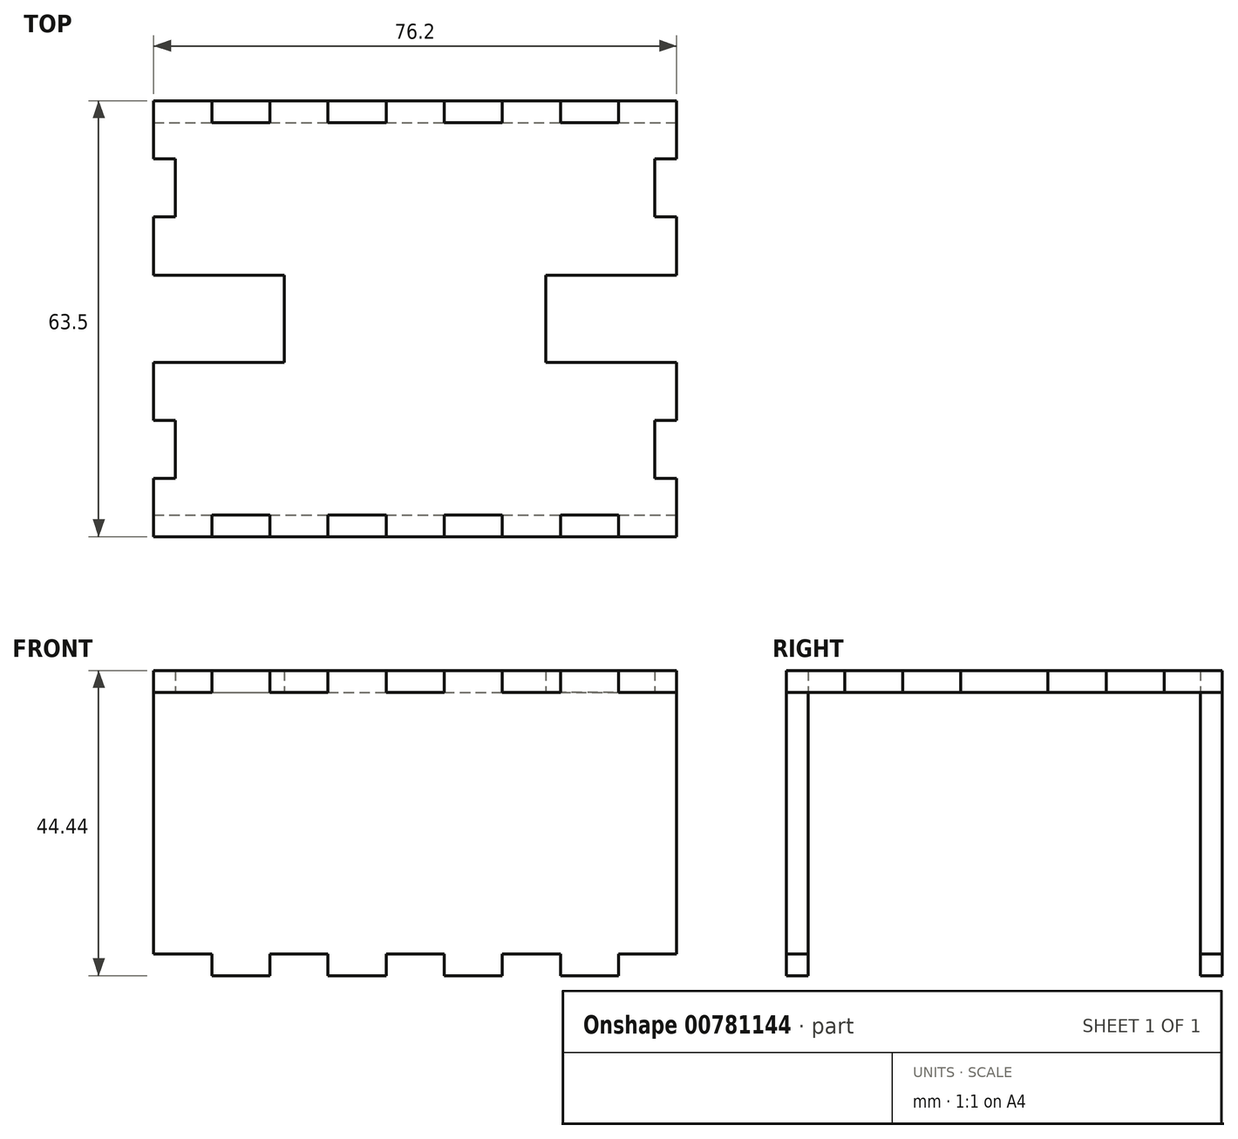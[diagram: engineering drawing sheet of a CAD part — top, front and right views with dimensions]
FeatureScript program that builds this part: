
annotation { "Feature Type Name" : "Feature", "Feature Type Description" : "" }
export const myFeature = defineFeature(function(context is Context, id is Id, definition is map)
    precondition{}
    {
        {
            var Q0;
            Q0=qCreatedBy(makeId("Top.planeOp"),FACE);
            var sketch = newSketch(context, id + "F0", { "sketchPlane" : qUnion([Q0])});
            skLineSegment(sketch, "E0.bottom", {"start": v(38.1, 31.75) * mm, "end": v(29.63, 31.75) * mm});
            skLineSegment(sketch, "E0.top", {"start": v(38.1, -31.75) * mm, "end": v(29.63, -31.75) * mm});
            skLineSegment(sketch, "E0.left", {"start": v(38.1, 31.75) * mm, "end": v(38.1, 23.28) * mm});
            skLineSegment(sketch, "E0.right", {"start": v(-38.1, 31.75) * mm, "end": v(-38.1, 23.28) * mm});
            skPoint(sketch, "E0.middle", {"position": v(0, 0) * mm});
            skLineSegment(sketch, "E1.bottom", {"start": v(-38.1, -31.75) * mm, "end": v(-29.63, -31.75) * mm});
            skLineSegment(sketch, "E1.top", {"start": v(-29.63, -28.58) * mm, "end": v(-21.17, -28.57) * mm});
            skLineSegment(sketch, "E1.right", {"start": v(38.1, -31.75) * mm, "end": v(38.1, -28.57) * mm});
            skLineSegment(sketch, "E2.right", {"start": v(-29.63, -28.58) * mm, "end": v(-29.63, -31.75) * mm});
            skLineSegment(sketch, "E3.bottom", {"start": v(-29.63, -28.58) * mm, "end": v(-21.17, -28.58) * mm});
            skLineSegment(sketch, "E3.right", {"start": v(-21.17, -28.57) * mm, "end": v(-21.17, -31.75) * mm});
            skLineSegment(sketch, "E4.top", {"start": v(-21.17, -31.75) * mm, "end": v(-12.7, -31.75) * mm});
            skLineSegment(sketch, "E4.left", {"start": v(-21.17, -28.58) * mm, "end": v(-21.17, -31.75) * mm});
            skLineSegment(sketch, "E4.right", {"start": v(-12.7, -28.58) * mm, "end": v(-12.7, -31.75) * mm});
            skLineSegment(sketch, "E5.bottom", {"start": v(-12.7, -28.58) * mm, "end": v(-4.23, -28.58) * mm});
            skLineSegment(sketch, "E5.right", {"start": v(-4.23, -28.58) * mm, "end": v(-4.23, -31.75) * mm});
            skLineSegment(sketch, "E6.top", {"start": v(-4.23, -31.75) * mm, "end": v(4.23, -31.75) * mm});
            skLineSegment(sketch, "E6.right", {"start": v(4.23, -28.58) * mm, "end": v(4.23, -31.75) * mm});
            skLineSegment(sketch, "E7.bottom", {"start": v(4.23, -28.58) * mm, "end": v(12.7, -28.58) * mm});
            skLineSegment(sketch, "E7.right", {"start": v(12.7, -28.57) * mm, "end": v(12.7, -31.75) * mm});
            skLineSegment(sketch, "E8.top", {"start": v(12.7, -31.75) * mm, "end": v(21.17, -31.75) * mm});
            skLineSegment(sketch, "E8.left", {"start": v(12.7, -28.58) * mm, "end": v(12.7, -31.75) * mm});
            skLineSegment(sketch, "E8.right", {"start": v(21.17, -28.58) * mm, "end": v(21.17, -31.75) * mm});
            skLineSegment(sketch, "E9.bottom", {"start": v(21.17, -28.58) * mm, "end": v(29.63, -28.58) * mm});
            skLineSegment(sketch, "E9.left", {"start": v(21.17, -28.57) * mm, "end": v(21.17, -31.75) * mm});
            skLineSegment(sketch, "E9.right", {"start": v(29.63, -28.57) * mm, "end": v(29.63, -31.75) * mm});
            skLineSegment(sketch, "E10.bottom", {"start": v(29.63, -31.75) * mm, "end": v(38.1, -31.75) * mm});
            skLineSegment(sketch, "E10.left", {"start": v(29.63, -31.75) * mm, "end": v(29.63, -28.57) * mm});
            skLineSegment(sketch, "E11.trimOffspring", {"start": v(-29.63, -31.75) * mm, "end": v(-38.1, -31.75) * mm});
            skLineSegment(sketch, "E12.trimOffspring", {"start": v(-12.7, -31.75) * mm, "end": v(-21.17, -31.75) * mm});
            skLineSegment(sketch, "E13.trimOffspring", {"start": v(4.23, -31.75) * mm, "end": v(-4.23, -31.75) * mm});
            skLineSegment(sketch, "E14.trimOffspring", {"start": v(21.17, -31.75) * mm, "end": v(12.7, -31.75) * mm});
            skLineSegment(sketch, "E15.MirrorCS", {"start": v(-29.63, 28.58) * mm, "end": v(-21.17, 28.58) * mm});
            skLineSegment(sketch, "E16.MirrorCS", {"start": v(-12.7, 28.58) * mm, "end": v(-4.23, 28.58) * mm});
            skLineSegment(sketch, "E17.MirrorCS", {"start": v(4.23, 28.58) * mm, "end": v(12.7, 28.58) * mm});
            skLineSegment(sketch, "E18.MirrorCS", {"start": v(21.17, 28.58) * mm, "end": v(29.63, 28.58) * mm});
            skLineSegment(sketch, "E19.MirrorCS", {"start": v(29.63, 31.75) * mm, "end": v(38.1, 31.75) * mm});
            skLineSegment(sketch, "E20.MirrorCS", {"start": v(21.17, 31.75) * mm, "end": v(12.7, 31.75) * mm});
            skLineSegment(sketch, "E21.MirrorCS", {"start": v(4.23, 31.75) * mm, "end": v(-4.23, 31.75) * mm});
            skLineSegment(sketch, "E22.MirrorCS", {"start": v(-21.17, 31.75) * mm, "end": v(-12.7, 31.75) * mm});
            skLineSegment(sketch, "E23.MirrorCS", {"start": v(-29.63, 31.75) * mm, "end": v(-38.1, 31.75) * mm});
            skLineSegment(sketch, "E24.MirrorCS", {"start": v(-29.63, 28.58) * mm, "end": v(-29.63, 31.75) * mm});
            skLineSegment(sketch, "E25.MirrorCS", {"start": v(-21.17, 28.58) * mm, "end": v(-21.17, 31.75) * mm});
            skLineSegment(sketch, "E26.MirrorCS", {"start": v(-12.7, 28.58) * mm, "end": v(-12.7, 31.75) * mm});
            skLineSegment(sketch, "E27.MirrorCS", {"start": v(-4.23, 28.58) * mm, "end": v(-4.23, 31.75) * mm});
            skLineSegment(sketch, "E28.MirrorCS", {"start": v(4.23, 28.58) * mm, "end": v(4.23, 31.75) * mm});
            skLineSegment(sketch, "E29.MirrorCS", {"start": v(12.7, 28.58) * mm, "end": v(12.7, 31.75) * mm});
            skLineSegment(sketch, "E30.MirrorCS", {"start": v(21.17, 28.58) * mm, "end": v(21.17, 31.75) * mm});
            skLineSegment(sketch, "E31.MirrorCS", {"start": v(29.63, 28.58) * mm, "end": v(29.63, 31.75) * mm});
            skLineSegment(sketch, "E32.MirrorCS", {"start": v(38.1, 31.75) * mm, "end": v(38.1, 28.57) * mm});
            skLineSegment(sketch, "E33.trimOffspring", {"start": v(-12.7, 31.75) * mm, "end": v(-21.17, 31.75) * mm});
            skLineSegment(sketch, "E34.trimOffspring", {"start": v(-12.7, -28.57) * mm, "end": v(-4.23, -28.57) * mm});
            skLineSegment(sketch, "E35.trimOffspring", {"start": v(4.23, -28.57) * mm, "end": v(12.7, -28.57) * mm});
            skLineSegment(sketch, "E36.trimOffspring", {"start": v(21.17, -28.57) * mm, "end": v(29.63, -28.57) * mm});
            skLineSegment(sketch, "E37.top", {"start": v(-38.12, -31.75) * mm, "end": v(-38.1, -31.75) * mm});
            skLineSegment(sketch, "E38", {"start": v(-34.92, -31.75) * mm, "end": v(-34.92, -6.35) * mm});
            skLineSegment(sketch, "E39.bottom", {"start": v(-38.1, 6.35) * mm, "end": v(-19.05, 6.35) * mm});
            skLineSegment(sketch, "E39.top", {"start": v(-38.1, -6.35) * mm, "end": v(-19.05, -6.35) * mm});
            skLineSegment(sketch, "E39.right", {"start": v(-19.05, 6.35) * mm, "end": v(-19.05, -6.35) * mm});
            skLineSegment(sketch, "E40", {"start": v(-38.1, 14.82) * mm, "end": v(-34.93, 14.82) * mm});
            skLineSegment(sketch, "E41", {"start": v(-38.1, 23.28) * mm, "end": v(-34.93, 23.28) * mm});
            skLineSegment(sketch, "E42", {"start": v(-38.1, 6.35) * mm, "end": v(-34.93, 6.35) * mm});
            skLineSegment(sketch, "E43", {"start": v(-38.1, -23.28) * mm, "end": v(-34.93, -23.28) * mm});
            skLineSegment(sketch, "E44", {"start": v(-34.93, -14.82) * mm, "end": v(-38.1, -14.82) * mm});
            skLineSegment(sketch, "E45", {"start": v(-38.1, -6.35) * mm, "end": v(-34.93, -6.35) * mm});
            skLineSegment(sketch, "E46.trimOffspring", {"start": v(-38.1, 14.82) * mm, "end": v(-38.1, 6.35) * mm});
            skLineSegment(sketch, "E47.trimOffspring", {"start": v(-38.1, -6.35) * mm, "end": v(-38.1, -14.82) * mm});
            skLineSegment(sketch, "E48.trimOffspring", {"start": v(-34.93, 6.35) * mm, "end": v(-34.93, 31.75) * mm});
            skLineSegment(sketch, "E49.trimOffspring", {"start": v(-38.1, -23.28) * mm, "end": v(-38.1, -31.75) * mm});
            skLineSegment(sketch, "E50.MirrorCS", {"start": v(38.1, 23.28) * mm, "end": v(34.93, 23.28) * mm});
            skLineSegment(sketch, "E51.MirrorCS", {"start": v(34.93, 6.35) * mm, "end": v(34.93, 31.75) * mm});
            skLineSegment(sketch, "E52.MirrorCS", {"start": v(38.1, 14.82) * mm, "end": v(34.93, 14.82) * mm});
            skLineSegment(sketch, "E53.MirrorCS", {"start": v(38.1, -6.35) * mm, "end": v(19.05, -6.35) * mm});
            skLineSegment(sketch, "E54.MirrorCS", {"start": v(38.1, 6.35) * mm, "end": v(19.05, 6.35) * mm});
            skLineSegment(sketch, "E55.MirrorCS", {"start": v(34.93, -14.82) * mm, "end": v(38.1, -14.82) * mm});
            skLineSegment(sketch, "E56.MirrorCS", {"start": v(19.05, 6.35) * mm, "end": v(19.05, -6.35) * mm});
            skLineSegment(sketch, "E57.MirrorCS", {"start": v(34.92, -31.75) * mm, "end": v(34.92, -6.35) * mm});
            skLineSegment(sketch, "E58.MirrorCS", {"start": v(38.1, -23.28) * mm, "end": v(34.93, -23.28) * mm});
            skLineSegment(sketch, "E59.trimOffspring", {"start": v(38.1, -23.28) * mm, "end": v(38.1, -31.75) * mm});
            skLineSegment(sketch, "E60.trimOffspring", {"start": v(38.1, -6.35) * mm, "end": v(38.1, -14.82) * mm});
            skLineSegment(sketch, "E61.trimOffspring", {"start": v(38.1, 14.82) * mm, "end": v(38.1, 6.35) * mm});
            skSolve(sketch);
        }
        {
            var Q0;
            Q0 = qSketchRegion(id + "F0", true);
            extrude(context, id + "F1", {"entities" : qUnion([Q0]), "depth" : 3.17 * mm, "offsetDistance" : 25.4 * mm});
        }
        {
            var Q0;
            Q0=makeQuery(id+"F1.opExtrude","SWEPT_FACE",FACE,{"disambiguationData":[OSD([sQuery(id+"F0.wireOp",EDGE,"E3.bottom")])]});
            var sketch = newSketch(context, id + "F2", { "sketchPlane" : qUnion([Q0])});
            skLineSegment(sketch, "E62.bottom", {"start": v(-29.63, 3.18) * mm, "end": v(-21.17, 3.18) * mm});
            skLineSegment(sketch, "E62.top", {"start": v(-29.63, -41.28) * mm, "end": v(-21.17, -41.28) * mm});
            skLineSegment(sketch, "E62.left", {"start": v(-38.1, 3.18) * mm, "end": v(-38.1, -41.28) * mm});
            skLineSegment(sketch, "E62.right", {"start": v(38.1, 3.18) * mm, "end": v(38.1, -41.28) * mm});
            skLineSegment(sketch, "E63.top", {"start": v(-38.1, 0) * mm, "end": v(38.1, 0) * mm});
            skLineSegment(sketch, "E63.left", {"start": v(-38.1, 3.18) * mm, "end": v(-38.1, 0) * mm});
            skLineSegment(sketch, "E63.right", {"start": v(38.1, 3.18) * mm, "end": v(38.1, 0) * mm});
            skLineSegment(sketch, "E64", {"start": v(-29.63, 3.18) * mm, "end": v(-29.63, 0) * mm});
            skLineSegment(sketch, "E65", {"start": v(-21.17, 0) * mm, "end": v(-21.17, 3.18) * mm});
            skLineSegment(sketch, "E66", {"start": v(-12.7, 3.18) * mm, "end": v(-12.7, 0) * mm});
            skLineSegment(sketch, "E67", {"start": v(-4.23, 0) * mm, "end": v(-4.23, 3.18) * mm});
            skLineSegment(sketch, "E68", {"start": v(4.23, 3.18) * mm, "end": v(4.23, 0) * mm});
            skLineSegment(sketch, "E69", {"start": v(12.7, 3.18) * mm, "end": v(12.7, 0) * mm});
            skLineSegment(sketch, "E70", {"start": v(21.17, 0) * mm, "end": v(21.17, 3.18) * mm});
            skLineSegment(sketch, "E71", {"start": v(29.63, 3.18) * mm, "end": v(29.63, 0) * mm});
            skLineSegment(sketch, "E72", {"start": v(38.1, 0) * mm, "end": v(38.1, 3.18) * mm});
            skLineSegment(sketch, "E73.trimOffspring", {"start": v(-12.7, 3.18) * mm, "end": v(-4.23, 3.18) * mm});
            skLineSegment(sketch, "E74.trimOffspring", {"start": v(4.23, 3.18) * mm, "end": v(12.7, 3.18) * mm});
            skLineSegment(sketch, "E75.trimOffspring", {"start": v(21.17, 3.18) * mm, "end": v(29.63, 3.18) * mm});
            skLineSegment(sketch, "E76.top", {"start": v(-38.1, -38.1) * mm, "end": v(38.1, -38.1) * mm});
            skLineSegment(sketch, "E76.left", {"start": v(-38.1, -41.28) * mm, "end": v(-38.1, -38.1) * mm});
            skLineSegment(sketch, "E76.right", {"start": v(38.1, -41.28) * mm, "end": v(38.1, -38.1) * mm});
            skLineSegment(sketch, "E77", {"start": v(-29.63, -38.1) * mm, "end": v(-29.63, -41.28) * mm});
            skLineSegment(sketch, "E78", {"start": v(-21.17, -38.1) * mm, "end": v(-21.17, -41.28) * mm});
            skLineSegment(sketch, "E79", {"start": v(-12.7, -41.28) * mm, "end": v(-12.7, -38.1) * mm});
            skLineSegment(sketch, "E80", {"start": v(-4.23, -38.1) * mm, "end": v(-4.23, -41.28) * mm});
            skLineSegment(sketch, "E81", {"start": v(4.23, -41.28) * mm, "end": v(4.23, -38.1) * mm});
            skLineSegment(sketch, "E82", {"start": v(12.7, -38.1) * mm, "end": v(12.7, -41.28) * mm});
            skLineSegment(sketch, "E83", {"start": v(21.17, -38.1) * mm, "end": v(21.17, -41.28) * mm});
            skLineSegment(sketch, "E84", {"start": v(29.63, -38.1) * mm, "end": v(29.63, -41.28) * mm});
            skLineSegment(sketch, "E85.trimOffspring", {"start": v(-12.7, -41.28) * mm, "end": v(-4.23, -41.28) * mm});
            skLineSegment(sketch, "E86.trimOffspring", {"start": v(4.23, -41.28) * mm, "end": v(12.7, -41.28) * mm});
            skLineSegment(sketch, "E87.trimOffspring", {"start": v(21.17, -41.28) * mm, "end": v(29.63, -41.28) * mm});
            skSolve(sketch);
        }
        {
            var Q0;
            Q0=makeQuery(id+"F2.imprint","IMPRINT",FACE,{"disambiguationData":[TD([[makeQuery(id+"F2.imprint","IMPRINT",EDGE,{"derivedFrom":sQuery(id+"F2.wireOp",EDGE,"E62.top")}),1.0]])]});
            var Q1;
            Q1=makeQuery(id+"F2.imprint","IMPRINT",FACE,{"disambiguationData":[TD([[makeQuery(id+"F2.imprint","IMPRINT",EDGE,{"derivedFrom":sQuery(id+"F2.wireOp",EDGE,"E62.bottom")}),-1.0]])]});
            var Q2;
            {var subQ0=sQuery(id+"F2.wireOp",EDGE,"E66");Q2=makeQuery(id+"F2.imprint","IMPRINT",FACE,{"disambiguationData":[TD([[makeQuery(id+"F2.imprint","IMPRINT",EDGE,{"derivedFrom":subQ0}),1.0]])]});}
            var Q3;
            {var subQ0=sQuery(id+"F2.wireOp",EDGE,"E68");Q3=makeQuery(id+"F2.imprint","IMPRINT",FACE,{"disambiguationData":[TD([[makeQuery(id+"F2.imprint","IMPRINT",EDGE,{"derivedFrom":subQ0}),1.0]])]});}
            var Q4;
            {var subQ0=sQuery(id+"F2.wireOp",EDGE,"E70");Q4=makeQuery(id+"F2.imprint","IMPRINT",FACE,{"disambiguationData":[TD([[makeQuery(id+"F2.imprint","IMPRINT",EDGE,{"derivedFrom":subQ0}),-1.0]])]});}
            var Q5;
            {var subQ16=sQuery(id+"F2.wireOp",EDGE,"E62.left");Q5=makeQuery(id+"F2.imprint","IMPRINT",FACE,{"disambiguationData":[TD([[makeQuery(id+"F2.imprint","IMPRINT",EDGE,{"derivedFrom":subQ16}),1.0]])]});}
            var Q6;
            Q6=makeQuery(id+"F2.imprint","IMPRINT",FACE,{"disambiguationData":[TD([[makeQuery(id+"F2.imprint","IMPRINT",EDGE,{"derivedFrom":sQuery(id+"F2.wireOp",EDGE,"E62.top")}),1.0]])]});
            var Q7;
            {var subQ0=sQuery(id+"F2.wireOp",EDGE,"E79");Q7=makeQuery(id+"F2.imprint","IMPRINT",FACE,{"disambiguationData":[TD([[makeQuery(id+"F2.imprint","IMPRINT",EDGE,{"derivedFrom":subQ0}),-1.0]])]});}
            var Q8;
            {var subQ0=sQuery(id+"F2.wireOp",EDGE,"E81");Q8=makeQuery(id+"F2.imprint","IMPRINT",FACE,{"disambiguationData":[TD([[makeQuery(id+"F2.imprint","IMPRINT",EDGE,{"derivedFrom":subQ0}),-1.0]])]});}
            var Q9;
            {var subQ0=sQuery(id+"F2.wireOp",EDGE,"E83");Q9=makeQuery(id+"F2.imprint","IMPRINT",FACE,{"disambiguationData":[TD([[makeQuery(id+"F2.imprint","IMPRINT",EDGE,{"derivedFrom":subQ0}),1.0]])]});}
            extrude(context, id + "F3", {"entities" : qUnion([Q0, Q1, Q2, Q3, Q4, Q5, Q6, Q7, Q8, Q9]), "depth" : 3.17 * mm, "offsetDistance" : 25.4 * mm});
        }
        {
            var Q0;
            Q0=makeQuery(id+"F3.opExtrude","SWEPT_BODY",BODY,{"disambiguationData":[OSD([sQuery(id+"F2.wireOp",EDGE,"E62.top"),sQuery(id+"F2.wireOp",EDGE,"E62.left"),sQuery(id+"F2.wireOp",EDGE,"E62.right"),sQuery(id+"F2.wireOp",EDGE,"E62.bottom"),sQuery(id+"F2.wireOp",EDGE,"E63.top"),sQuery(id+"F2.wireOp",EDGE,"E64"),sQuery(id+"F2.wireOp",EDGE,"E65"),sQuery(id+"F2.wireOp",EDGE,"E66"),sQuery(id+"F2.wireOp",EDGE,"E67"),sQuery(id+"F2.wireOp",EDGE,"E68"),sQuery(id+"F2.wireOp",EDGE,"E69"),sQuery(id+"F2.wireOp",EDGE,"E70"),sQuery(id+"F2.wireOp",EDGE,"E71"),sQuery(id+"F2.wireOp",EDGE,"E73.trimOffspring"),sQuery(id+"F2.wireOp",EDGE,"E74.trimOffspring"),sQuery(id+"F2.wireOp",EDGE,"E75.trimOffspring")])]});
            var Q1;
            Q1=qCreatedBy(makeId("Front.planeOp"),FACE);
            mirror(context, id + "F4", {"entities" : qUnion([Q0]), "mirrorPlane" : qUnion([Q1])});
        }
    });
